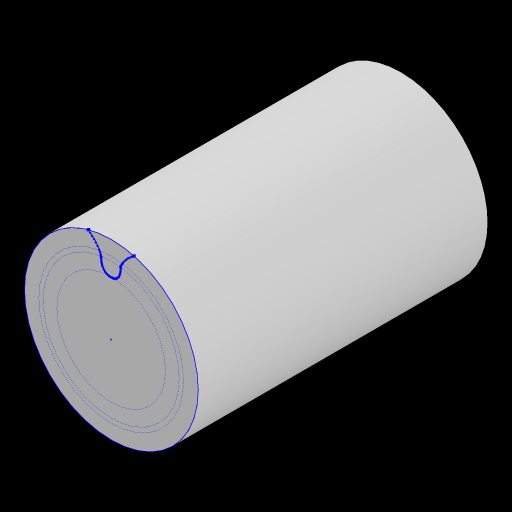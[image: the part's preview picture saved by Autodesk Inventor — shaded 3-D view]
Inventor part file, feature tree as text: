
AUTODESK INVENTOR PART (.ipt)
format: ipt  version: 2023.2 (Build 272271030, 271C)  size: 107,008 bytes
history: native  units: mm
features: sketch x1, extrude x1
ambient origin geometry x8: Origin, YZ Plane, XZ Plane, XY Plane, X Axis, Y Axis, Z Axis, Center Point
bodies: Solid1 (feature_tree)
feature tree (2):
  sketch  "Sketch1"  dims[d0=20.0mm d1=0.0mm]
  extrude  "Extrusion1"  TaperAngle=0.0deg  [1 undecoded]
note: 1 required parameter value undecoded (feature->parameter linkage not recoverable at this tier; creation-order binding heuristic only, values carry confidence <= 0.55)
